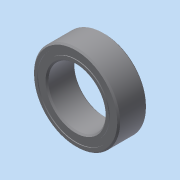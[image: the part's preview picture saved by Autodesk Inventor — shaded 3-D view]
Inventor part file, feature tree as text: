
AUTODESK INVENTOR PART (.ipt)
format: ipt  version: 2015 (Build 190159000, 159)  size: 594,432 bytes
history: native  units: in
note: dims shown in document units (in); Inventor stores cm internally (conversion verified against a paired STEP export)
features: imported_body x16, other x12, revolve x5
ambient origin geometry x8: Origin, YZ Plane, XZ Plane, XY Plane, X Axis, Y Axis, Z Axis, Center Point
bodies: Body1 (feature_tree), Body2 (feature_tree), Body3 (feature_tree), Body4 (feature_tree), Body5 (feature_tree), Body6 (feature_tree), Body7 (feature_tree), Body8 (feature_tree), Body9 (feature_tree), Body10 (feature_tree), Body11 (feature_tree), Body12 (feature_tree), Body13 (feature_tree), Body14 (feature_tree), Body15 (feature_tree), Body16 (feature_tree)
feature tree (33):
  revolve  "Revolve1"  [1 undecoded]
  other  "57155K3751"
  revolve  "Revolve3"  [1 undecoded]
  revolve  "Revolve4"  [1 undecoded]
  other  "CirPattern1[1]"
  other  "CirPattern1[2]"
  other  "CirPattern1[3]"
  other  "CirPattern1[4]"
  other  "CirPattern1[5]"
  other  "CirPattern1[6]"
  other  "CirPattern1[7]"
  other  "CirPattern1[8]"
  other  "CirPattern1[9]"
  other  "CirPattern1[10]"
  other  "CirPattern1[11]"
  revolve  "Revolve5[1]"  [1 undecoded]
  revolve  "Revolve5[2]"  [1 undecoded]
  imported_body  "Base1"
  imported_body  "Base2"
  imported_body  "Base3"
  imported_body  "Base4"
  imported_body  "Base5"
  imported_body  "Base6"
  imported_body  "Base7"
  imported_body  "Base8"
  imported_body  "Base9"
  imported_body  "Base10"
  imported_body  "Base11"
  imported_body  "Base12"
  imported_body  "Base13"
  imported_body  "Base14"
  imported_body  "Base15"
  imported_body  "Base16"
note: 5 required parameter values undecoded (feature->parameter linkage not recoverable at this tier; creation-order binding heuristic only, values carry confidence <= 0.55)
